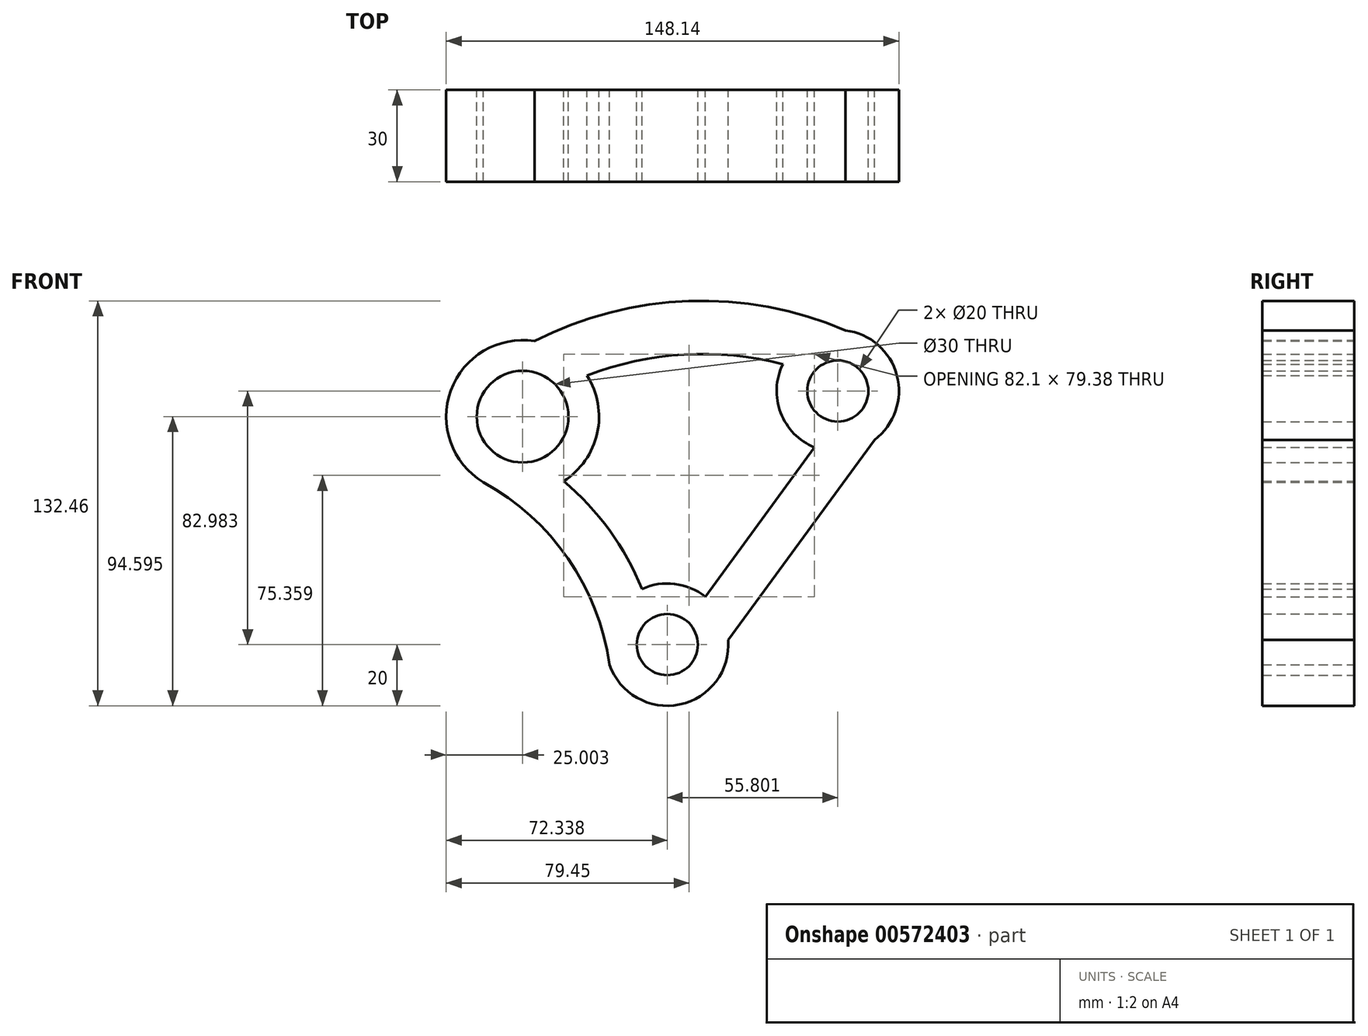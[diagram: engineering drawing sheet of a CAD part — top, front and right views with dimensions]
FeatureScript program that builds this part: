
annotation { "Feature Type Name" : "Feature", "Feature Type Description" : "" }
export const myFeature = defineFeature(function(context is Context, id is Id, definition is map)
    precondition{}
    {
        {
            var Q0;
            Q0=qCreatedBy(makeId("Front.planeOp"),FACE);
            var sketch = newSketch(context, id + "F0", { "sketchPlane" : qUnion([Q0])});
            skCircle(sketch, "E0", {"center": v(-32.12, 21.45) * mm, "radius": 15 * mm});
            skCircle(sketch, "E1", {"center": v(71.02, 29.84) * mm, "radius": 10 * mm});
            skCircle(sketch, "E2", {"center": v(15.22, -53.14) * mm, "radius": 10 * mm});
            skArc(sketch, "E3", {"start": v(-18.72, 0.35) * mm, "mid": v(-7.71, 16.03) * mm, "end": v(-11.04, 34.9) * mm});
            skArc(sketch, "E4", {"start": v(83.05, 13.87) * mm, "mid": v(90.35, 34.97) * mm, "end": v(73.55, 49.68) * mm});
            skArc(sketch, "E5", {"start": v(-4.78, -53.65) * mm, "mid": v(16.25, -73.11) * mm, "end": v(35.16, -51.58) * mm});
            skLineSegment(sketch, "E6", {"start": v(63.38, 11.36) * mm, "end": v(27.65, -37.47) * mm});
            skLineSegment(sketch, "E7", {"start": v(83.05, 13.87) * mm, "end": v(35.16, -51.58) * mm});
            skLineSegment(sketch, "E8", {"start": v(15.22, -53.14) * mm, "end": v(15.22, 74.42) * mm, "construction": true});
            skLineSegment(sketch, "E9", {"start": v(-32.12, 21.45) * mm, "end": v(15.22, -53.14) * mm, "construction": true});
            skLineSegment(sketch, "E10", {"start": v(71.02, 29.84) * mm, "end": v(15.22, -53.14) * mm, "construction": true});
            skArc(sketch, "E11", {"start": v(73.55, 49.68) * mm, "mid": v(22.27, 59.25) * mm, "end": v(-28.22, 46.15) * mm});
            skArc(sketch, "E12", {"start": v(71.08, 39.84) * mm, "mid": v(9.2, 47.9) * mm, "end": v(-47.1, 20.98) * mm, "construction": true});
            skArc(sketch, "E13", {"start": v(-3.69, -59.67) * mm, "mid": v(-17.27, -24.96) * mm, "end": v(-44.95, 0) * mm});
            skArc(sketch, "E14", {"start": v(6.95, -34.93) * mm, "mid": v(-3.71, -15.71) * mm, "end": v(-18.72, 0.35) * mm});
            skArc(sketch, "E15.trimOffspring", {"start": v(53.03, 38.59) * mm, "mid": v(52.32, 22.74) * mm, "end": v(63.38, 11.36) * mm});
            skArc(sketch, "E16.trimOffspring", {"start": v(-28.22, 46.15) * mm, "mid": v(-55.85, 29.3) * mm, "end": v(-43.72, -0.7) * mm});
            skArc(sketch, "E17", {"start": v(53.03, 38.59) * mm, "mid": v(20.7, 41.76) * mm, "end": v(-11.04, 34.9) * mm});
            skArc(sketch, "E18.trimOffspring", {"start": v(27.65, -37.47) * mm, "mid": v(17.66, -33.29) * mm, "end": v(6.95, -34.93) * mm});
            skSolve(sketch);
        }
        {
            var Q0;
            Q0=makeQuery(id+"F0.imprint","IMPRINT",FACE,{"disambiguationData":[TD([[makeQuery(id+"F0.imprint","IMPRINT",EDGE,{"derivedFrom":sQuery(id+"F0.wireOp",EDGE,"E0")}),-1.0]])]});
            extrude(context, id + "F1", {"entities" : qUnion([Q0]), "depth" : 30 * mm, "offsetDistance" : 25 * mm});
        }
    });
